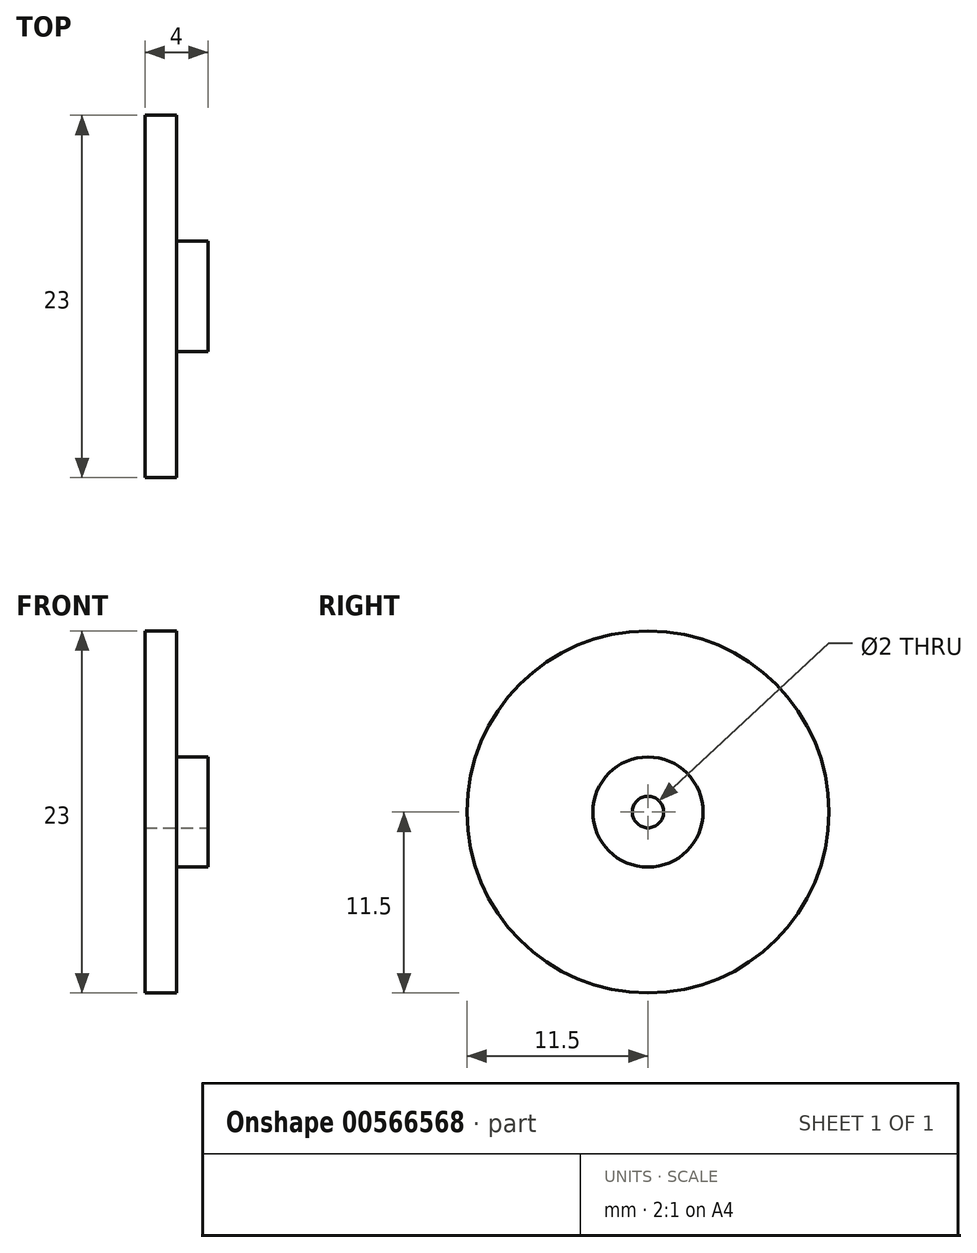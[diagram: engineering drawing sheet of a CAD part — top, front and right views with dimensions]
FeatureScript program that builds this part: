
annotation { "Feature Type Name" : "Feature", "Feature Type Description" : "" }
export const myFeature = defineFeature(function(context is Context, id is Id, definition is map)
    precondition{}
    {
        {
            var Q0;
            Q0=qCreatedBy(makeId("Right.planeOp"),FACE);
            var sketch = newSketch(context, id + "F0", { "sketchPlane" : qUnion([Q0])});
            skCircle(sketch, "E0", {"center": v(0, 0) * mm, "radius": 11.5 * mm});
            skSolve(sketch);
        }
        {
            var Q0;
            Q0 = qSketchRegion(id + "F0", true);
            extrude(context, id + "F1", {"entities" : qUnion([Q0]), "depth" : 2 * mm, "offsetDistance" : 25 * mm});
        }
        {
            var Q0;
            Q0=makeQuery(id+"F1.opExtrude","CAP_FACE",FACE,{"disambiguationData":[OSD([sQuery(id+"F0.wireOp",EDGE,"E0")])],"isStart":false});
            var sketch = newSketch(context, id + "F2", { "sketchPlane" : qUnion([Q0])});
            skCircle(sketch, "E1", {"center": v(0, 0) * mm, "radius": 3.5 * mm});
            skSolve(sketch);
        }
        {
            var Q0;
            Q0 = qSketchRegion(id + "F2", true);
            extrude(context, id + "F3", {"entities" : qUnion([Q0]), "operationType" : NewBodyOperationType.ADD, "depth" : 2 * mm, "offsetDistance" : 25 * mm});
        }
        {
            var Q0;
            Q0=makeQuery(id+"F3.opExtrude","CAP_FACE",FACE,{"disambiguationData":[OSD([sQuery(id+"F2.wireOp",EDGE,"E1")])],"isStart":false});
            var sketch = newSketch(context, id + "F4", { "sketchPlane" : qUnion([Q0])});
            skCircle(sketch, "E2", {"center": v(0, 0) * mm, "radius": 1 * mm});
            skSolve(sketch);
        }
        {
            var Q0;
            Q0 = qSketchRegion(id + "F4", true);
            extrude(context, id + "F5", {"entities" : qUnion([Q0]), "operationType" : NewBodyOperationType.REMOVE, "endBound" : BoundingType.THROUGH_ALL, "oppositeDirection" : true, "depth" : 25 * mm, "offsetDistance" : 25 * mm});
        }
    });
